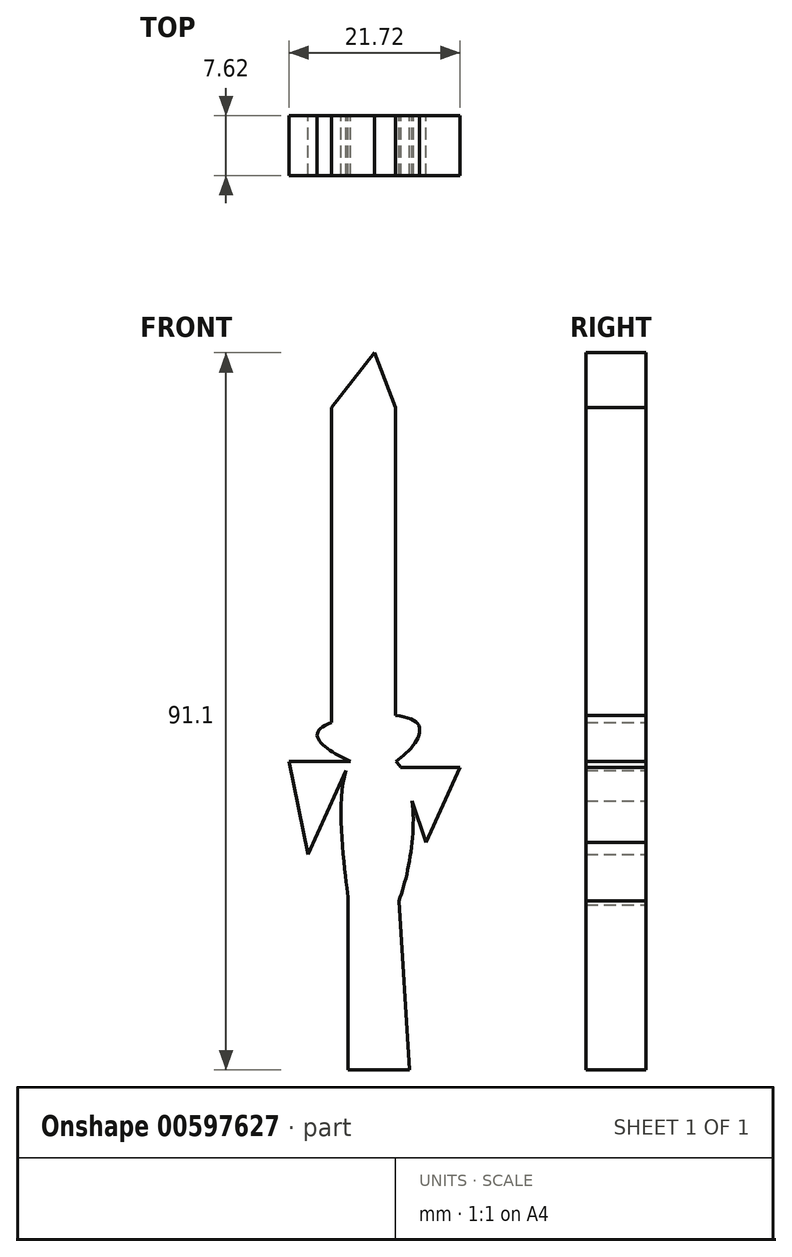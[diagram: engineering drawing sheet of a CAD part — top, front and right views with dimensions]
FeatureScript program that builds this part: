
annotation { "Feature Type Name" : "Feature", "Feature Type Description" : "" }
export const myFeature = defineFeature(function(context is Context, id is Id, definition is map)
    precondition{}
    {
        {
            var Q0;
            Q0=qCreatedBy(makeId("Front.planeOp"),FACE);
            var sketch = newSketch(context, id + "F0", { "sketchPlane" : qUnion([Q0])});
            skFitSpline(sketch, "E0", {"points": [v(-3.09, -14.63) * mm, v(-3.36, -32.62) * mm, v(-3.36, -32.9) * mm, v(0, -35.3) * mm, v(3.09, -32.35) * mm, v(3.36, -15.44) * mm, v(-3.09, -14.63) * mm]});
            skLineSegment(sketch, "E1", {"start": v(-3.36, -32.9) * mm, "end": v(-3.36, -53.83) * mm});
            skLineSegment(sketch, "E2", {"start": v(-3.36, -53.83) * mm, "end": v(4.43, -53.83) * mm});
            skLineSegment(sketch, "E3", {"start": v(4.43, -53.83) * mm, "end": v(3.09, -32.35) * mm});
            skLineSegment(sketch, "E4", {"start": v(-3.09, -14.63) * mm, "end": v(-8.46, -26.45) * mm});
            skLineSegment(sketch, "E5", {"start": v(-8.46, -26.45) * mm, "end": v(-10.87, -14.63) * mm});
            skLineSegment(sketch, "E6", {"start": v(-10.87, -14.63) * mm, "end": v(-3.09, -14.63) * mm});
            skLineSegment(sketch, "E7", {"start": v(3.36, -15.44) * mm, "end": v(10.85, -15.44) * mm});
            skLineSegment(sketch, "E8", {"start": v(10.85, -15.44) * mm, "end": v(6.52, -24.96) * mm});
            skLineSegment(sketch, "E9", {"start": v(6.52, -24.96) * mm, "end": v(3.36, -15.44) * mm});
            skFitSpline(sketch, "E10", {"points": [v(-3.09, -14.63) * mm, v(-7.12, -10.73) * mm, v(5.34, -9.7) * mm, v(2.7, -14.63) * mm, v(-3.09, -14.63) * mm]});
            skLineSegment(sketch, "E11", {"start": v(-5.49, -9.7) * mm, "end": v(-5.49, 30.33) * mm});
            skLineSegment(sketch, "E12", {"start": v(-5.49, 30.33) * mm, "end": v(0, 37.27) * mm});
            skLineSegment(sketch, "E13", {"start": v(0, 37.27) * mm, "end": v(2.68, 30.33) * mm});
            skLineSegment(sketch, "E14", {"start": v(2.68, 30.33) * mm, "end": v(2.68, -8.8) * mm});
            skSolve(sketch);
        }
        {
            var Q0;
            Q0 = qSketchRegion(id + "F0", true);
            extrude(context, id + "F1", {"entities" : qUnion([Q0]), "depth" : 7.62 * mm, "offsetDistance" : 25.4 * mm});
        }
    });
